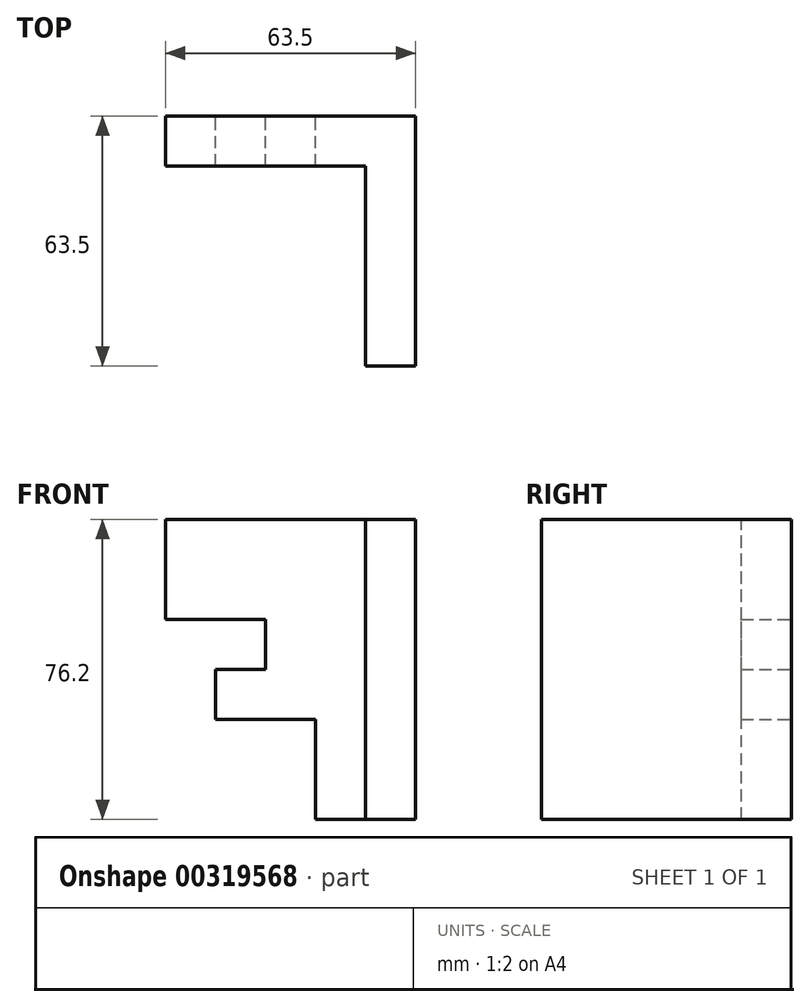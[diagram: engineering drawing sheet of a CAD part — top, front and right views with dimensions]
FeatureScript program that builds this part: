
annotation { "Feature Type Name" : "Feature", "Feature Type Description" : "" }
export const myFeature = defineFeature(function(context is Context, id is Id, definition is map)
    precondition{}
    {
        {
            var Q0;
            Q0=qCreatedBy(makeId("Front.planeOp"),FACE);
            var sketch = newSketch(context, id + "F0", { "sketchPlane" : qUnion([Q0])});
            skLineSegment(sketch, "E0", {"start": v(-27.2, 33.76) * mm, "end": v(36.3, 33.76) * mm});
            skLineSegment(sketch, "E1", {"start": v(36.3, 33.76) * mm, "end": v(36.3, -42.44) * mm});
            skLineSegment(sketch, "E2", {"start": v(36.3, -42.44) * mm, "end": v(10.9, -42.44) * mm});
            skLineSegment(sketch, "E3", {"start": v(10.9, -42.44) * mm, "end": v(10.9, -17.04) * mm});
            skLineSegment(sketch, "E4", {"start": v(10.9, -17.04) * mm, "end": v(-14.5, -17.04) * mm});
            skLineSegment(sketch, "E5", {"start": v(-14.5, -17.04) * mm, "end": v(-14.5, -4.34) * mm});
            skLineSegment(sketch, "E6", {"start": v(-14.5, -4.34) * mm, "end": v(-1.8, -4.34) * mm});
            skLineSegment(sketch, "E7", {"start": v(-1.8, -4.34) * mm, "end": v(-1.8, 8.36) * mm});
            skLineSegment(sketch, "E8", {"start": v(-1.8, 8.36) * mm, "end": v(-27.2, 8.36) * mm});
            skLineSegment(sketch, "E9", {"start": v(-27.2, 8.36) * mm, "end": v(-27.2, 33.76) * mm});
            skSolve(sketch);
        }
        {
            var Q0;
            Q0=makeQuery(id+"F0.imprint","IMPRINT",FACE,{"disambiguationData":[TD([[makeQuery(id+"F0.imprint","IMPRINT",EDGE,{"derivedFrom":sQuery(id+"F0.wireOp",EDGE,"E0")}),-1.0]])]});
            extrude(context, id + "F1", {"entities" : qUnion([Q0]), "depth" : 12.7 * mm});
        }
        {
            var Q0;
            Q0=makeQuery(id+"F1.opExtrude","CAP_FACE",FACE,{"disambiguationData":[OSD([sQuery(id+"F0.wireOp",EDGE,"E0"),sQuery(id+"F0.wireOp",EDGE,"E1"),sQuery(id+"F0.wireOp",EDGE,"E2"),sQuery(id+"F0.wireOp",EDGE,"E3"),sQuery(id+"F0.wireOp",EDGE,"E4"),sQuery(id+"F0.wireOp",EDGE,"E5"),sQuery(id+"F0.wireOp",EDGE,"E6"),sQuery(id+"F0.wireOp",EDGE,"E7"),sQuery(id+"F0.wireOp",EDGE,"E8"),sQuery(id+"F0.wireOp",EDGE,"E9")])],"isStart":false});
            var sketch = newSketch(context, id + "F2", { "sketchPlane" : qUnion([Q0])});
            skLineSegment(sketch, "E10", {"start": v(36.3, 33.76) * mm, "end": v(23.6, 33.76) * mm});
            skLineSegment(sketch, "E11", {"start": v(36.3, -42.44) * mm, "end": v(23.6, -42.44) * mm});
            skLineSegment(sketch, "E12", {"start": v(23.6, -42.44) * mm, "end": v(23.6, 33.76) * mm});
            skLineSegment(sketch, "E13", {"start": v(36.3, 33.76) * mm, "end": v(36.3, -42.44) * mm});
            skSolve(sketch);
        }
        {
            var Q0;
            Q0=makeQuery(id+"F2.imprint","IMPRINT",FACE,{"disambiguationData":[TD([[makeQuery(id+"F2.imprint","IMPRINT",EDGE,{"derivedFrom":sQuery(id+"F2.wireOp",EDGE,"E10")}),-1.0]])]});
            extrude(context, id + "F3", {"entities" : qUnion([Q0]), "operationType" : NewBodyOperationType.ADD, "depth" : 50.8 * mm});
        }
    });
